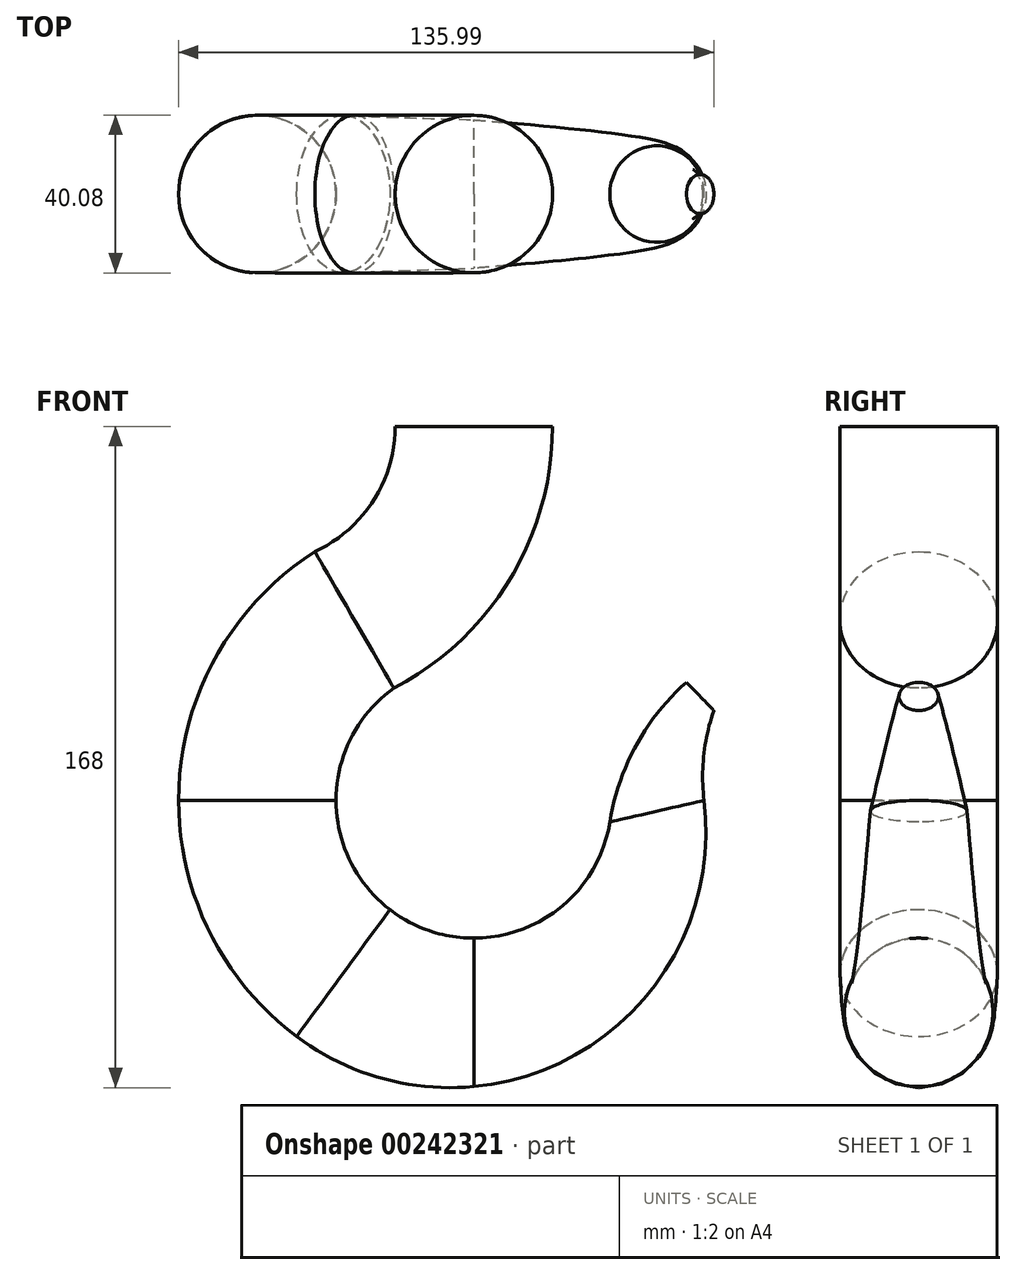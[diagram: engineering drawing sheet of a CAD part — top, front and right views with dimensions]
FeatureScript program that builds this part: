
annotation { "Feature Type Name" : "Feature", "Feature Type Description" : "" }
export const myFeature = defineFeature(function(context is Context, id is Id, definition is map)
    precondition{}
    {
        {
            var Q0;
            Q0=qCreatedBy(makeId("Front.planeOp"),FACE);
            var sketch = newSketch(context, id + "F0", { "sketchPlane" : qUnion([Q0])});
            skLineSegment(sketch, "E0", {"start": v(-114.02, -95) * mm, "end": v(122.17, -95) * mm, "construction": true});
            skLineSegment(sketch, "E1", {"start": v(0, 73.01) * mm, "end": v(0, -301.68) * mm, "construction": true});
            skLineSegment(sketch, "E2", {"start": v(20, 0) * mm, "end": v(-20, 0) * mm});
            skPoint(sketch, "E3", {"position": v(0, 0) * mm});
            skArc(sketch, "E4", {"start": v(-40.4, -31.8) * mm, "mid": v(-25.54, -18.9) * mm, "end": v(-20, 0) * mm});
            skArc(sketch, "E5", {"start": v(20, 0) * mm, "mid": v(9.14, -38.88) * mm, "end": v(-20.3, -66.5) * mm});
            skPoint(sketch, "E6", {"position": v(0, -95) * mm});
            skArc(sketch, "E7", {"start": v(-20.3, -66.5) * mm, "mid": v(-18.43, -124.75) * mm, "end": v(34.57, -100.49) * mm});
            skArc(sketch, "E8", {"start": v(-40.4, -31.8) * mm, "mid": v(-74.95, -92.2) * mm, "end": v(-45, -155) * mm});
            skArc(sketch, "E9", {"start": v(-45, -155) * mm, "mid": v(26.6, -159.23) * mm, "end": v(58.5, -95) * mm});
            skArc(sketch, "E10", {"start": v(54.02, -65) * mm, "mid": v(41.2, -81.05) * mm, "end": v(34.57, -100.49) * mm});
            skLineSegment(sketch, "E11", {"start": v(54.02, -65) * mm, "end": v(60.99, -72.17) * mm});
            skArc(sketch, "E12", {"start": v(60.99, -72.17) * mm, "mid": v(58.42, -83.44) * mm, "end": v(58.5, -95) * mm});
            skLineSegment(sketch, "E13", {"start": v(-40.4, -31.8) * mm, "end": v(-20.3, -66.5) * mm});
            skLineSegment(sketch, "E14", {"start": v(-75, -95) * mm, "end": v(-35, -95) * mm});
            skLineSegment(sketch, "E15", {"start": v(0, -130) * mm, "end": v(0, -167.72) * mm});
            skLineSegment(sketch, "E16", {"start": v(34.57, -100.49) * mm, "end": v(58.5, -95) * mm});
            skLineSegment(sketch, "E17", {"start": v(-45, -155) * mm, "end": v(-21.31, -122.76) * mm});
            skSolve(sketch);
        }
        {
            var Q0;
            Q0=qCreatedBy(makeId("Top.planeOp"),FACE);
            var sketch = newSketch(context, id + "F1", { "sketchPlane" : qUnion([Q0])});
            skLineSegment(sketch, "E18.0", {"start": v(20, 0) * mm, "end": v(-20, 0) * mm, "construction": true});
            skCircle(sketch, "E19", {"center": v(0, 0) * mm, "radius": 20 * mm});
            skSolve(sketch);
        }
        {
            var Q0;
            Q0=sQuery(id+"F0.wireOp",EDGE,"E11");
            cPlane(context, id + "F2", {"entities" : qUnion([Q0]), "cplaneType" : CPlaneType.LINE_ANGLE, "offset" : 25 * mm, "angle" : 90 * degree, "width" : 150 * mm, "height" : 150 * mm});
        }
        {
            var Q0;
            Q0=qCreatedBy(id+"F2.planeOp",FACE);
            var sketch = newSketch(context, id + "F3", { "sketchPlane" : qUnion([Q0])});
            skLineSegment(sketch, "E20.0", {"start": v(0, -84.25) * mm, "end": v(0, -94.25) * mm, "construction": true});
            skCircle(sketch, "E21", {"center": v(0, -89.25) * mm, "radius": 5 * mm});
            skSolve(sketch);
        }
        {
            var Q0;
            Q0=qCreatedBy(makeId("Top.planeOp"),FACE);
            cPlane(context, id + "F4", {"entities" : qUnion([Q0]), "cplaneType" : CPlaneType.OFFSET, "offset" : 95 * mm, "oppositeDirection" : true, "width" : 150 * mm, "height" : 150 * mm});
        }
        {
            var Q0;
            Q0=qCreatedBy(id+"F4.planeOp",FACE);
            var sketch = newSketch(context, id + "F5", { "sketchPlane" : qUnion([Q0])});
            skLineSegment(sketch, "E22.0", {"start": v(-40.4, 0) * mm, "end": v(-75, 0) * mm, "construction": true});
            skLineSegment(sketch, "E23.0", {"start": v(-35, 0) * mm, "end": v(34.57, 0) * mm, "construction": true});
            skLineSegment(sketch, "E24", {"start": v(-75, 0) * mm, "end": v(-35, 0) * mm, "construction": true});
            skCircle(sketch, "E25", {"center": v(-55, 0) * mm, "radius": 20 * mm});
            skSolve(sketch);
        }
        {
            var Q0;
            Q0=qCreatedBy(makeId("Right.planeOp"),FACE);
            var sketch = newSketch(context, id + "F6", { "sketchPlane" : qUnion([Q0])});
            skLineSegment(sketch, "E26.0", {"start": v(0, -130) * mm, "end": v(0, -167.72) * mm, "construction": true});
            skCircle(sketch, "E27", {"center": v(0, -148.86) * mm, "radius": 18.86 * mm});
            skSolve(sketch);
        }
        {
            var Q0;
            Q0=sQuery(id+"F0.wireOp",EDGE,"E13");
            cPlane(context, id + "F7", {"entities" : qUnion([Q0]), "cplaneType" : CPlaneType.LINE_ANGLE, "offset" : 25 * mm, "angle" : 0 * degree, "width" : 150 * mm, "height" : 150 * mm});
        }
        {
            var Q0;
            Q0=qCreatedBy(id+"F7.planeOp",FACE);
            var sketch = newSketch(context, id + "F8", { "sketchPlane" : qUnion([Q0])});
            skPoint(sketch, "E28.0", {"position": v(0, -27.33) * mm});
            skPoint(sketch, "E29.0", {"position": v(0, -7.29) * mm});
            skCircle(sketch, "E30", {"center": v(0, -27.33) * mm, "radius": 20.04 * mm});
            skSolve(sketch);
        }
        {
            var Q0;
            {var subQ0=sQuery(id+"F0.wireOp",EDGE,"E13");Q0=makeQuery(id+"F0.imprint","IMPRINT",FACE,{"disambiguationData":[TD([[makeQuery(id+"F0.imprint","IMPRINT",EDGE,{"derivedFrom":subQ0}),-1.0]])]});}
            var sketch = newSketch(context, id + "F9", { "sketchPlane" : qUnion([Q0])});
            skLineSegment(sketch, "E31.0.0", {"start": v(-20.3, -66.5) * mm, "end": v(-40.4, -31.8) * mm});
            skArc(sketch, "E31.0.1", {"start": v(-40.4, -31.8) * mm, "mid": v(-65.78, -58.97) * mm, "end": v(-75, -95) * mm});
            skLineSegment(sketch, "E31.0.2", {"start": v(-75, -95) * mm, "end": v(-35, -95) * mm});
            skArc(sketch, "E31.0.3", {"start": v(-35, -95) * mm, "mid": v(-31.11, -78.97) * mm, "end": v(-20.3, -66.5) * mm});
            skSolve(sketch);
        }
        {
            var Q0;
            Q0=makeQuery(id+"F8.imprint","IMPRINT",FACE,{"disambiguationData":[TD([[makeQuery(id+"F8.imprint","IMPRINT",EDGE,{"derivedFrom":sQuery(id+"F8.wireOp",EDGE,"E30")}),1.0]])]});
            var Q1;
            Q1=makeQuery(id+"F5.imprint","IMPRINT",FACE,{"disambiguationData":[TD([[makeQuery(id+"F5.imprint","IMPRINT",EDGE,{"derivedFrom":sQuery(id+"F5.wireOp",EDGE,"E25")}),1.0]])]});
            var Q2;
            Q2=sQuery(id+"F9.wireOp",EDGE,"E31.0.1");
            var Q3;
            Q3=sQuery(id+"F9.wireOp",EDGE,"E31.0.3");
            loft(context, id + "F10", {"addGuides" : true, "sheetProfilesArray" : [{ "sheetProfileEntities" : qUnion([Q0]) }, { "sheetProfileEntities" : qUnion([Q1]) }], "guidesArray" : [{ "guideEntities" : qUnion([Q2]), "guideDerivativeType" : LoftGuideDerivativeType.DEFAULT, "guideDerivativeMagnitude" : 1 }, { "guideEntities" : qUnion([Q3]), "guideDerivativeType" : LoftGuideDerivativeType.DEFAULT, "guideDerivativeMagnitude" : 1 }]});
        }
        {
            var Q0;
            Q0=sQuery(id+"F0.wireOp",EDGE,"E16");
            cPlane(context, id + "F11", {"entities" : qUnion([Q0]), "cplaneType" : CPlaneType.LINE_ANGLE, "offset" : 25 * mm, "angle" : 90 * degree, "width" : 150 * mm, "height" : 150 * mm});
        }
        {
            var Q0;
            Q0=qCreatedBy(id+"F11.planeOp",FACE);
            var sketch = newSketch(context, id + "F12", { "sketchPlane" : qUnion([Q0])});
            skPoint(sketch, "E32.0", {"position": v(23.53, 0) * mm});
            skPoint(sketch, "E33.0", {"position": v(11.25, 0) * mm});
            skCircle(sketch, "E34", {"center": v(23.53, 0) * mm, "radius": 12.28 * mm});
            skSolve(sketch);
        }
        {
            var Q0;
            {var subQ2=sQuery(id+"F0.wireOp",EDGE,"E15");Q0=makeQuery(id+"F0.imprint","IMPRINT",FACE,{"disambiguationData":[TD([[makeQuery(id+"F0.imprint","IMPRINT",EDGE,{"derivedFrom":subQ2}),1.0]])]});}
            var sketch = newSketch(context, id + "F13", { "sketchPlane" : qUnion([Q0])});
            skLineSegment(sketch, "E35.0.0", {"start": v(58.5, -95) * mm, "end": v(34.57, -100.49) * mm});
            skArc(sketch, "E35.0.1", {"start": v(34.57, -100.49) * mm, "mid": v(22.73, -121.62) * mm, "end": v(0, -130) * mm});
            skLineSegment(sketch, "E35.0.2", {"start": v(0, -130) * mm, "end": v(0, -167.72) * mm});
            skArc(sketch, "E35.0.3", {"start": v(0, -167.72) * mm, "mid": v(44.64, -143.74) * mm, "end": v(58.5, -95) * mm});
            skSolve(sketch);
        }
        {
            var Q0;
            Q0=makeQuery(id+"F12.imprint","IMPRINT",FACE,{"disambiguationData":[TD([[makeQuery(id+"F12.imprint","IMPRINT",EDGE,{"derivedFrom":sQuery(id+"F12.wireOp",EDGE,"E34")}),1.0]])]});
            var Q1;
            Q1=makeQuery(id+"F6.imprint","IMPRINT",FACE,{"disambiguationData":[TD([[makeQuery(id+"F6.imprint","IMPRINT",EDGE,{"derivedFrom":sQuery(id+"F6.wireOp",EDGE,"E27")}),1.0]])]});
            var Q2;
            Q2=sQuery(id+"F13.wireOp",EDGE,"E35.0.1");
            var Q3;
            Q3=sQuery(id+"F13.wireOp",EDGE,"E35.0.3");
            loft(context, id + "F14", {"addGuides" : true, "sheetProfilesArray" : [{ "sheetProfileEntities" : qUnion([Q0]) }, { "sheetProfileEntities" : qUnion([Q1]) }], "guidesArray" : [{ "guideEntities" : qUnion([Q2]), "guideDerivativeType" : LoftGuideDerivativeType.DEFAULT, "guideDerivativeMagnitude" : 1 }, { "guideEntities" : qUnion([Q3]), "guideDerivativeType" : LoftGuideDerivativeType.DEFAULT, "guideDerivativeMagnitude" : 1 }]});
        }
        {
            var Q0;
            Q0=makeQuery(id+"F0.imprint","IMPRINT",FACE,{"disambiguationData":[TD([[makeQuery(id+"F0.imprint","IMPRINT",EDGE,{"derivedFrom":sQuery(id+"F0.wireOp",EDGE,"E10")}),1.0]])]});
            var sketch = newSketch(context, id + "F15", { "sketchPlane" : qUnion([Q0])});
            skArc(sketch, "E36.0.0", {"start": v(54.02, -65) * mm, "mid": v(41.2, -81.05) * mm, "end": v(34.57, -100.49) * mm});
            skLineSegment(sketch, "E36.0.1", {"start": v(34.57, -100.49) * mm, "end": v(58.5, -95) * mm});
            skArc(sketch, "E36.0.2", {"start": v(58.5, -95) * mm, "mid": v(58.42, -83.44) * mm, "end": v(60.99, -72.17) * mm});
            skLineSegment(sketch, "E36.0.3", {"start": v(60.99, -72.17) * mm, "end": v(54.02, -65) * mm});
            skSolve(sketch);
        }
        {
            var Q1;
            Q1=makeQuery(id+"F3.imprint","IMPRINT",FACE,{"disambiguationData":[TD([[makeQuery(id+"F3.imprint","IMPRINT",EDGE,{"derivedFrom":sQuery(id+"F3.wireOp",EDGE,"E21")}),1.0]])]});
            var Q2;
            Q2=makeQuery(id+"F14.opLoft","CAP_FACE",FACE,{"disambiguationData":[OSD([makeQuery(id+"F12.imprint","IMPRINT",FACE,{"disambiguationData":[TD([[makeQuery(id+"F12.imprint","IMPRINT",EDGE,{"derivedFrom":sQuery(id+"F12.wireOp",EDGE,"E34")}),1.0]])]})])],"isStart":true});
            var Q3;
            Q3=sQuery(id+"F15.wireOp",EDGE,"E36.0.0");
            var Q4;
            Q4=sQuery(id+"F15.wireOp",EDGE,"E36.0.2");
            loft(context, id + "F16", {"operationType" : NewBodyOperationType.ADD, "addGuides" : true, "sheetProfilesArray" : [{ "sheetProfileEntities" : qUnion([Q1]) }, { "sheetProfileEntities" : qUnion([Q2]) }], "guidesArray" : [{ "guideEntities" : qUnion([Q3]), "guideDerivativeType" : LoftGuideDerivativeType.DEFAULT, "guideDerivativeMagnitude" : 1 }, { "guideEntities" : qUnion([Q4]), "guideDerivativeType" : LoftGuideDerivativeType.DEFAULT, "guideDerivativeMagnitude" : 1 }]});
        }
        {
            var Q0;
            Q0=sQuery(id+"F0.wireOp",EDGE,"E17");
            cPlane(context, id + "F17", {"entities" : qUnion([Q0]), "cplaneType" : CPlaneType.LINE_ANGLE, "offset" : 25 * mm, "angle" : 0 * degree, "width" : 150 * mm, "height" : 150 * mm});
        }
        {
            var Q0;
            Q0=qCreatedBy(id+"F17.planeOp",FACE);
            var sketch = newSketch(context, id + "F18", { "sketchPlane" : qUnion([Q0])});
            skLineSegment(sketch, "E37.0", {"start": v(0, -151.56) * mm, "end": v(0, -111.55) * mm, "construction": true});
            skCircle(sketch, "E38", {"center": v(0, -131.55) * mm, "radius": 20 * mm});
            skSolve(sketch);
        }
        {
            var Q0;
            {var subQ0=sQuery(id+"F0.wireOp",EDGE,"E14");Q0=makeQuery(id+"F0.imprint","IMPRINT",FACE,{"disambiguationData":[TD([[makeQuery(id+"F0.imprint","IMPRINT",EDGE,{"derivedFrom":subQ0}),-1.0]])]});}
            var sketch = newSketch(context, id + "F19", { "sketchPlane" : qUnion([Q0])});
            skArc(sketch, "E39.0.0", {"start": v(-75, -95) * mm, "mid": v(-67.08, -128.54) * mm, "end": v(-45, -155) * mm});
            skLineSegment(sketch, "E39.0.1", {"start": v(-45, -155) * mm, "end": v(-21.31, -122.76) * mm});
            skArc(sketch, "E39.0.2", {"start": v(-21.31, -122.76) * mm, "mid": v(-31.4, -110.48) * mm, "end": v(-35, -95) * mm});
            skLineSegment(sketch, "E39.0.3", {"start": v(-35, -95) * mm, "end": v(-75, -95) * mm});
            skSolve(sketch);
        }
        {
            var Q0;
            {var subQ0=sQuery(id+"F0.wireOp",EDGE,"E15");Q0=makeQuery(id+"F0.imprint","IMPRINT",FACE,{"disambiguationData":[TD([[makeQuery(id+"F0.imprint","IMPRINT",EDGE,{"derivedFrom":subQ0}),-1.0]])]});}
            var sketch = newSketch(context, id + "F20", { "sketchPlane" : qUnion([Q0])});
            skArc(sketch, "E40.0.0", {"start": v(0, -130) * mm, "mid": v(-11.26, -128.14) * mm, "end": v(-21.31, -122.76) * mm});
            skLineSegment(sketch, "E40.0.1", {"start": v(-21.31, -122.76) * mm, "end": v(-45, -155) * mm});
            skArc(sketch, "E40.0.2", {"start": v(-45, -155) * mm, "mid": v(-23.68, -165.55) * mm, "end": v(0, -167.72) * mm});
            skLineSegment(sketch, "E40.0.3", {"start": v(0, -167.72) * mm, "end": v(0, -130) * mm});
            skSolve(sketch);
        }
        {
            var Q1;
            Q1=makeQuery(id+"F14.opLoft","CAP_FACE",FACE,{"disambiguationData":[OSD([makeQuery(id+"F6.imprint","IMPRINT",FACE,{"disambiguationData":[TD([[makeQuery(id+"F6.imprint","IMPRINT",EDGE,{"derivedFrom":sQuery(id+"F6.wireOp",EDGE,"E27")}),1.0]])]})])],"isStart":true});
            var Q2;
            Q2=makeQuery(id+"F18.imprint","IMPRINT",FACE,{"disambiguationData":[TD([[makeQuery(id+"F18.imprint","IMPRINT",EDGE,{"derivedFrom":sQuery(id+"F18.wireOp",EDGE,"E38")}),1.0]])]});
            var Q3;
            Q3=sQuery(id+"F20.wireOp",EDGE,"E40.0.0");
            var Q4;
            Q4=sQuery(id+"F20.wireOp",EDGE,"E40.0.2");
            loft(context, id + "F21", {"operationType" : NewBodyOperationType.ADD, "addGuides" : true, "sheetProfilesArray" : [{ "sheetProfileEntities" : qUnion([Q1]) }, { "sheetProfileEntities" : qUnion([Q2]) }], "guidesArray" : [{ "guideEntities" : qUnion([Q3]), "guideDerivativeType" : LoftGuideDerivativeType.DEFAULT, "guideDerivativeMagnitude" : 1 }, { "guideEntities" : qUnion([Q4]), "guideDerivativeType" : LoftGuideDerivativeType.DEFAULT, "guideDerivativeMagnitude" : 1 }]});
        }
        {
            var Q0;
            Q0=makeQuery(id+"F21.opLoft","CAP_FACE",FACE,{"disambiguationData":[OSD([makeQuery(id+"F18.imprint","IMPRINT",FACE,{"disambiguationData":[TD([[makeQuery(id+"F18.imprint","IMPRINT",EDGE,{"derivedFrom":sQuery(id+"F18.wireOp",EDGE,"E38")}),1.0]])]})])],"isStart":true});
            var Q1;
            Q1=makeQuery(id+"F10.opLoft","CAP_FACE",FACE,{"disambiguationData":[OSD([makeQuery(id+"F5.imprint","IMPRINT",FACE,{"disambiguationData":[TD([[makeQuery(id+"F5.imprint","IMPRINT",EDGE,{"derivedFrom":sQuery(id+"F5.wireOp",EDGE,"E25")}),1.0]])]})])],"isStart":true});
            var Q2;
            Q2=sQuery(id+"F19.wireOp",EDGE,"E39.0.2");
            var Q3;
            Q3=sQuery(id+"F19.wireOp",EDGE,"E39.0.0");
            loft(context, id + "F22", {"addGuides" : true, "sheetProfilesArray" : [{ "sheetProfileEntities" : qUnion([Q0]) }, { "sheetProfileEntities" : qUnion([Q1]) }], "guidesArray" : [{ "guideEntities" : qUnion([Q2]), "guideDerivativeType" : LoftGuideDerivativeType.DEFAULT, "guideDerivativeMagnitude" : 1 }, { "guideEntities" : qUnion([Q3]), "guideDerivativeType" : LoftGuideDerivativeType.DEFAULT, "guideDerivativeMagnitude" : 1 }]});
        }
        {
            var Q1;
            Q1=makeQuery(id+"F1.imprint","IMPRINT",FACE,{"disambiguationData":[TD([[makeQuery(id+"F1.imprint","IMPRINT",EDGE,{"derivedFrom":sQuery(id+"F1.wireOp",EDGE,"E19")}),1.0]])]});
            var Q2;
            Q2=makeQuery(id+"F10.opLoft","CAP_FACE",FACE,{"disambiguationData":[OSD([makeQuery(id+"F8.imprint","IMPRINT",FACE,{"disambiguationData":[TD([[makeQuery(id+"F8.imprint","IMPRINT",EDGE,{"derivedFrom":sQuery(id+"F8.wireOp",EDGE,"E30")}),1.0]])]})])],"isStart":true});
            var Q3;
            Q3=sQuery(id+"F0.wireOp",EDGE,"E5");
            var Q4;
            Q4=sQuery(id+"F0.wireOp",EDGE,"E4");
            loft(context, id + "F23", {"operationType" : NewBodyOperationType.ADD, "addGuides" : true, "sheetProfilesArray" : [{ "sheetProfileEntities" : qUnion([Q1]) }, { "sheetProfileEntities" : qUnion([Q2]) }], "guidesArray" : [{ "guideEntities" : qUnion([Q3]), "guideDerivativeType" : LoftGuideDerivativeType.DEFAULT, "guideDerivativeMagnitude" : 1 }, { "guideEntities" : qUnion([Q4]), "guideDerivativeType" : LoftGuideDerivativeType.DEFAULT, "guideDerivativeMagnitude" : 1 }]});
        }
    });
